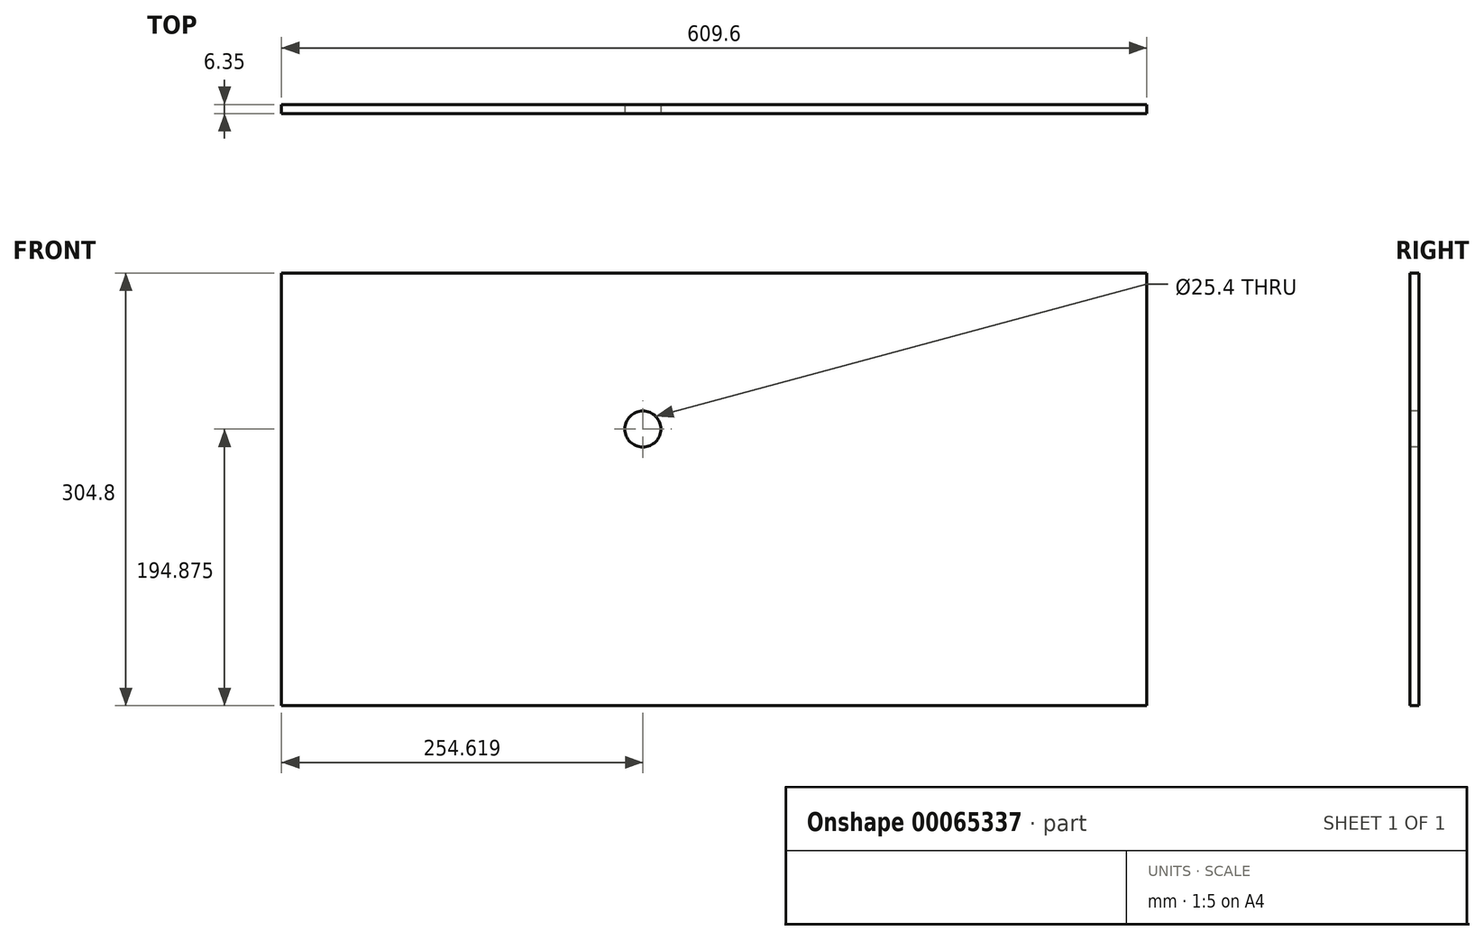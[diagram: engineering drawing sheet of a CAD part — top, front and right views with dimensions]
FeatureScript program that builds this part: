
annotation { "Feature Type Name" : "Feature", "Feature Type Description" : "" }
export const myFeature = defineFeature(function(context is Context, id is Id, definition is map)
    precondition{}
    {
        {
            var Q0;
            Q0=qCreatedBy(makeId("Front.planeOp"),FACE);
            var sketch = newSketch(context, id + "F0", { "sketchPlane" : qUnion([Q0])});
            skLineSegment(sketch, "E0.bottom", {"start": v(0, 0) * mm, "end": v(609.6, 0) * mm});
            skLineSegment(sketch, "E0.top", {"start": v(0, -304.8) * mm, "end": v(609.6, -304.8) * mm});
            skLineSegment(sketch, "E0.left", {"start": v(0, 0) * mm, "end": v(0, -304.8) * mm});
            skLineSegment(sketch, "E0.right", {"start": v(609.6, 0) * mm, "end": v(609.6, -304.8) * mm});
            skSolve(sketch);
        }
        {
            var Q0;
            Q0=makeQuery(id+"F0.imprint","IMPRINT",FACE,{"disambiguationData":[TD([[makeQuery(id+"F0.imprint","IMPRINT",EDGE,{"derivedFrom":sQuery(id+"F0.wireOp",EDGE,"E0.bottom")}),-1.0]])]});
            extrude(context, id + "F1", {"entities" : qUnion([Q0]), "depth" : 6.35 * mm});
        }
        {
            var Q0;
            Q0=makeQuery(id+"F1.opExtrude","CAP_FACE",FACE,{"disambiguationData":[OSD([sQuery(id+"F0.wireOp",EDGE,"E0.bottom"),sQuery(id+"F0.wireOp",EDGE,"E0.top"),sQuery(id+"F0.wireOp",EDGE,"E0.left"),sQuery(id+"F0.wireOp",EDGE,"E0.right")])],"isStart":false});
            var sketch = newSketch(context, id + "F2", { "sketchPlane" : qUnion([Q0])});
            skCircle(sketch, "E1", {"center": v(254.62, -109.92) * mm, "radius": 12.7 * mm});
            skSolve(sketch);
        }
        {
            var Q0;
            Q0 = qSketchRegion(id + "F2", true);
            extrude(context, id + "F3", {"entities" : qUnion([Q0]), "operationType" : NewBodyOperationType.REMOVE, "oppositeDirection" : true, "depth" : 25.4 * mm});
        }
    });
